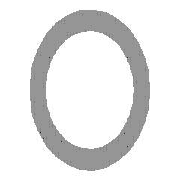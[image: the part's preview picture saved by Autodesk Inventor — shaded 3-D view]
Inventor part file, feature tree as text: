
AUTODESK INVENTOR PART (.ipt)
format: ipt  version: 2021 (Build 250183000, 183)  size: 752,640 bytes
history: native  units: mm (DEFAULTED — no unit token found)
features: other x15, plane x4, sketch x4, split x2, sweep x1
ambient origin geometry x8: Origin, YZ Plane, XZ Plane, XY Plane, X Axis, Y Axis, Z Axis, Center Point
bodies: Solid1 (feature_tree)
feature tree (26):
  parser-record x1  (decoder bookkeeping rows leaked as tree rows — omitted from the tree; the rows remain in map.json)
  other  "Driven Length"
  other  "Plano inicial"
  other  "Plano final"
  other  "Trayectoria de barrido"
  plane  "Plano de trabajo de orientación"
  sweep  "Cuerpo"
  plane  "Plano de trabajo5"
  split  "Dividir1"
  plane  "Plano de trabajo6"
  split  "Dividir2"
  sketch  "Sketch3"  dims[d0=26.67mm d1=2.8702mm]
  plane  "Work Plane3"
  sketch  "Sketch4"  dims[d4=-0.0mm]
  sketch  "Boceto5"  dims[d5=1207.483196mm]
  other  "Sup1"
  sketch  "Boceto6"  dims[d6=90.0deg d7=1207.483196mm d8=0.0mm d9=0.0mm d10=0.0mm d11=90.0deg d12=0.0mm d13=90.0deg d22=16.002mm d23=53.080004mm d24=0.0mm d25=90.0deg d26=0.0mm d27=90.0deg d28=5.0mm d29=0.0mm d30=5.0mm d31=0.0mm]
  other  "Sup8"
  other  "Sup10"
  other  "Sup11"
  other  "Sólido4"
  other  "SuperficieSolevación1"
  other  "SuperficieSolevación2"
  other  "Sup9"
  other  "Superficie de contorno5"
  other  "Superficie de contorno6"
